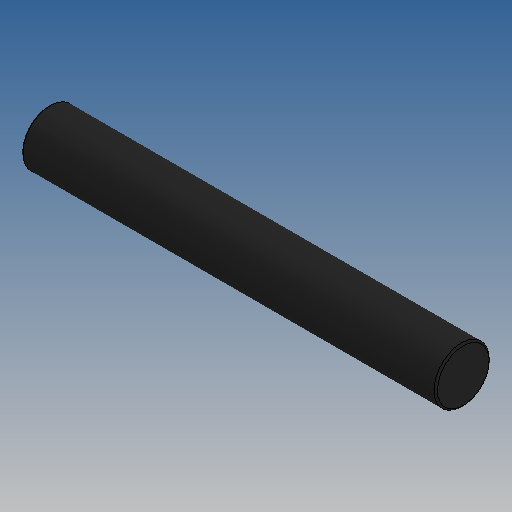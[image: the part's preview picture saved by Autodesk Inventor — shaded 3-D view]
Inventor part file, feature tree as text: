
AUTODESK INVENTOR PART (.ipt)
format: ipt  version: 2025 (Build 290162010, 162A)  size: 134,144 bytes
history: native  units: mm (DEFAULTED — no unit token found)
features: extrude x1, fillet x1, sketch x1
ambient origin geometry x8: Origin, YZ Plane, XZ Plane, XY Plane, X Axis, Y Axis, Z Axis, Center Point
bodies: Solid2 (feature_tree)
feature tree (3):
  extrude  "Extrusion7"  Depth=24.0mm TaperAngle=0.0deg
  fillet  "Fillet2"  Radius=0.1mm
  sketch  "Sketch1"  dims[d26=3.2mm d27=24.0mm d28=0.0mm d29=0.1mm d30=0.0mm d31=0.0mm]
